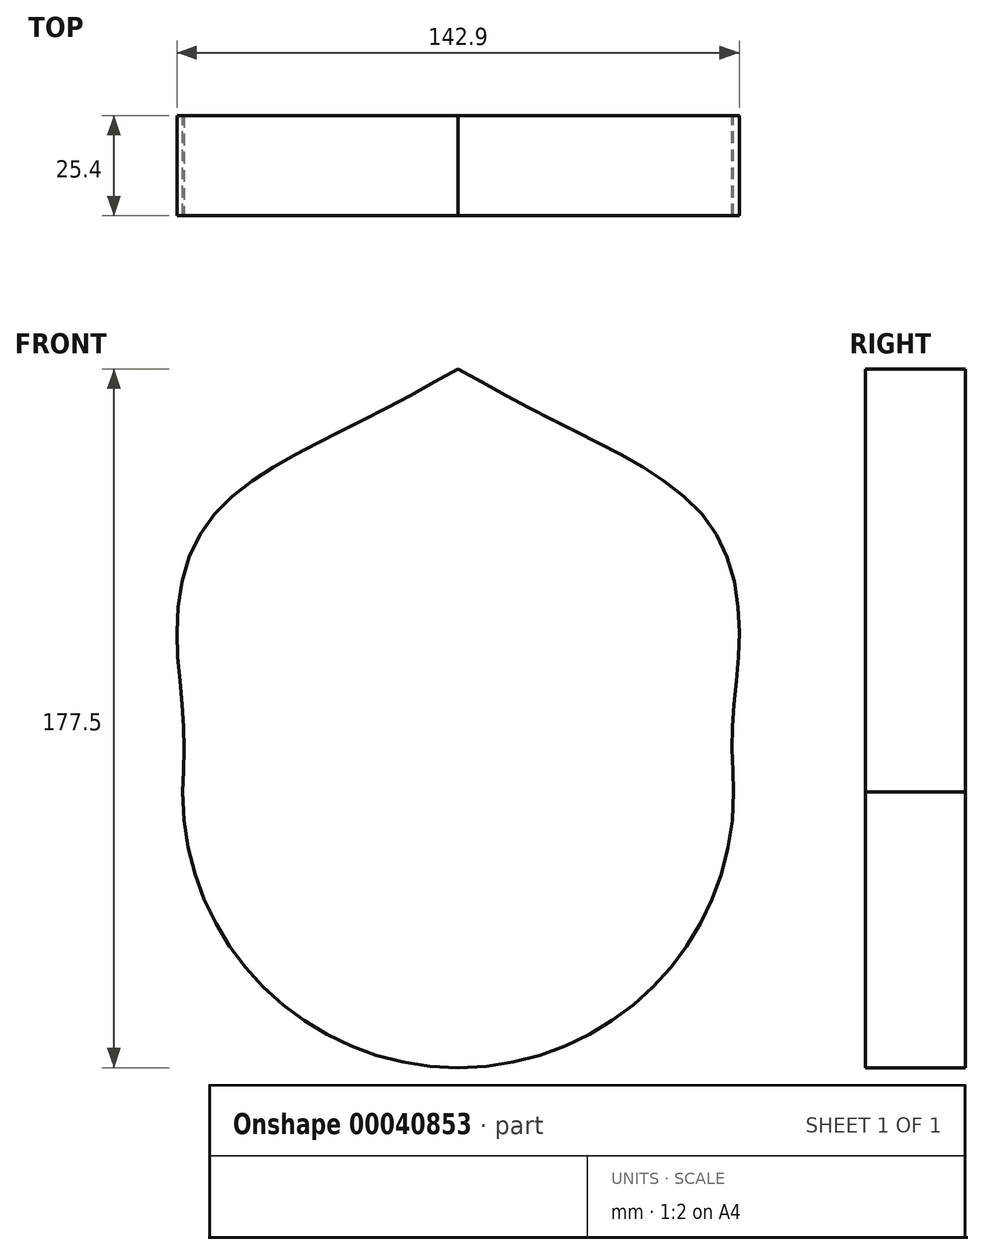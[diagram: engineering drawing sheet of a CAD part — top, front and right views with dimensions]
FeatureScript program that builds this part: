
annotation { "Feature Type Name" : "Feature", "Feature Type Description" : "" }
export const myFeature = defineFeature(function(context is Context, id is Id, definition is map)
    precondition{}
    {
        {
            var Q0;
            Q0=qCreatedBy(makeId("Front.planeOp"),FACE);
            var sketch = newSketch(context, id + "F0", { "sketchPlane" : qUnion([Q0])});
            skFitSpline(sketch, "E0", {"points": [v(70, 0) * mm, v(69.8, 18.7) * mm, v(71.45, 41.25) * mm, v(65.57, 65.57) * mm, v(47.5, 82.27) * mm, v(25.18, 93.96) * mm, v(0, 107.5) * mm], "startDerivative": vector(-6.03, 124.92) * mm, "endDerivative": vector(-140.01, 77.56) * mm});
            skFitSpline(sketch, "E1.MirrorCS", {"points": [v(-70, 0) * mm, v(-69.8, 18.7) * mm, v(-71.45, 41.25) * mm, v(-65.57, 65.57) * mm, v(-47.5, 82.27) * mm, v(-25.18, 93.96) * mm, v(0, 107.5) * mm], "startDerivative": vector(6.03, 124.92) * mm, "endDerivative": vector(140.01, 77.56) * mm});
            skArc(sketch, "E2", {"start": v(-70, 0) * mm, "mid": v(0, -70) * mm, "end": v(70, 0) * mm});
            skSolve(sketch);
        }
        {
            var Q0;
            Q0 = qSketchRegion(id + "F0", true);
            extrude(context, id + "F1", {"entities" : qUnion([Q0]), "depth" : 25.4 * mm});
        }
    });
